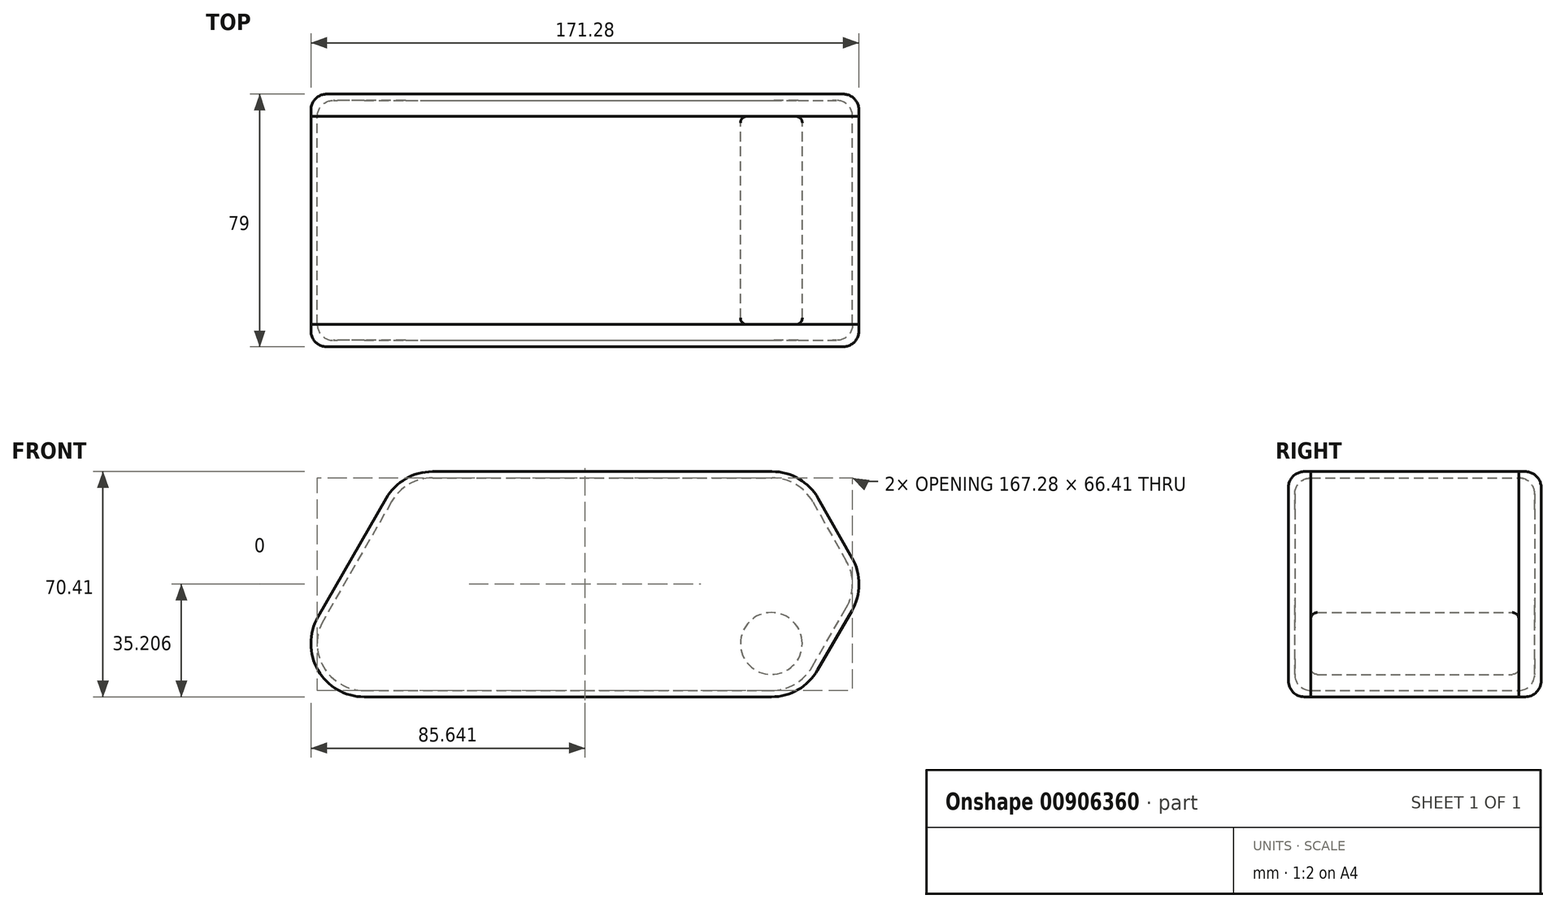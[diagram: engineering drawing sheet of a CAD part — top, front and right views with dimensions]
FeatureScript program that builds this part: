
annotation { "Feature Type Name" : "Feature", "Feature Type Description" : "" }
export const myFeature = defineFeature(function(context is Context, id is Id, definition is map)
    precondition{}
    {
        {
            var Q0;
            Q0=qCreatedBy(makeId("Front.planeOp"),FACE);
            var sketch = newSketch(context, id + "F0", { "sketchPlane" : qUnion([Q0])});
            skCircle(sketch, "E0.1.0.0", {"center": v(20, 0) * mm, "radius": 9.67 * mm});
            skCircle(sketch, "E0.1.1.0", {"center": v(30.7, 18.54) * mm, "radius": 9.67 * mm});
            skCircle(sketch, "E0.2.0.0", {"center": v(41.2, 0) * mm, "radius": 9.67 * mm});
            skCircle(sketch, "E0.2.1.0", {"center": v(51.9, 18.54) * mm, "radius": 9.67 * mm});
            skCircle(sketch, "E0.2.2.0", {"center": v(62.6, 37.07) * mm, "radius": 9.67 * mm});
            skCircle(sketch, "E0.3.0.0", {"center": v(62.41, 0) * mm, "radius": 9.67 * mm});
            skCircle(sketch, "E0.3.1.0", {"center": v(73.11, 18.54) * mm, "radius": 9.67 * mm});
            skCircle(sketch, "E0.3.2.0", {"center": v(83.82, 37.07) * mm, "radius": 9.67 * mm});
            skCircle(sketch, "E0.4.0.0", {"center": v(83.62, 0) * mm, "radius": 9.67 * mm});
            skCircle(sketch, "E0.4.1.0", {"center": v(94.32, 18.54) * mm, "radius": 9.67 * mm});
            skCircle(sketch, "E0.4.2.0", {"center": v(105.02, 37.07) * mm, "radius": 9.67 * mm});
            skCircle(sketch, "E0.5.0.0", {"center": v(104.83, 0) * mm, "radius": 9.67 * mm});
            skCircle(sketch, "E0.5.1.0", {"center": v(115.53, 18.54) * mm, "radius": 9.67 * mm});
            skCircle(sketch, "E0.5.2.0", {"center": v(126.23, 37.07) * mm, "radius": 9.67 * mm});
            skCircle(sketch, "E0.6.0.0", {"center": v(126.03, 0) * mm, "radius": 9.67 * mm});
            skCircle(sketch, "E0.6.1.0", {"center": v(136.74, 18.54) * mm, "radius": 9.67 * mm});
            skCircle(sketch, "E0.6.2.0", {"center": v(147.44, 37.07) * mm, "radius": 9.67 * mm});
            skCircle(sketch, "E0.7.0.0", {"center": v(147.24, 0) * mm, "radius": 9.67 * mm});
            skCircle(sketch, "E0.7.1.0", {"center": v(157.94, 18.54) * mm, "radius": 9.67 * mm});
            skLineSegment(sketch, "E0.direction1", {"start": v(0, 0) * mm, "end": v(20, 0) * mm, "construction": true});
            skLineSegment(sketch, "E0.direction2", {"start": v(0, 0) * mm, "end": v(10.55, 18.27) * mm, "construction": true});
            skCircle(sketch, "E1.1.0.0", {"center": v(41.3, 37.05) * mm, "radius": 9.67 * mm});
            skLineSegment(sketch, "E1.direction1", {"start": v(62.6, 37.07) * mm, "end": v(41.3, 37.05) * mm, "construction": true});
            skSolve(sketch);
        }
        {
            var Q0;
            Q0=qCreatedBy(makeId("Front.planeOp"),FACE);
            var sketch = newSketch(context, id + "F1", { "sketchPlane" : qUnion([Q0])});
            skArc(sketch, "E2.0", {"start": v(41.3, 46.72) * mm, "mid": v(36.46, 45.42) * mm, "end": v(32.92, 41.87) * mm});
            skArc(sketch, "E3.0", {"start": v(11.62, 4.82) * mm, "mid": v(11.63, -4.84) * mm, "end": v(20, -9.67) * mm});
            skArc(sketch, "E4.0", {"start": v(147.24, -9.67) * mm, "mid": v(152.07, -8.37) * mm, "end": v(155.61, -4.83) * mm});
            skArc(sketch, "E5.0", {"start": v(166.32, 13.7) * mm, "mid": v(167.61, 18.5) * mm, "end": v(166.35, 23.3) * mm});
            skArc(sketch, "E6.0", {"start": v(155.85, 41.84) * mm, "mid": v(152.3, 45.43) * mm, "end": v(147.44, 46.74) * mm});
            skLineSegment(sketch, "E7", {"start": v(32.92, 41.87) * mm, "end": v(11.62, 4.82) * mm});
            skLineSegment(sketch, "E8", {"start": v(41.3, 46.72) * mm, "end": v(147.44, 46.74) * mm});
            skLineSegment(sketch, "E9", {"start": v(155.85, 41.84) * mm, "end": v(166.35, 23.3) * mm});
            skLineSegment(sketch, "E10", {"start": v(155.61, -4.83) * mm, "end": v(166.32, 13.7) * mm});
            skLineSegment(sketch, "E11", {"start": v(20, -9.67) * mm, "end": v(147.24, -9.67) * mm});
            skArc(sketch, "E12.0", {"start": v(41.3, 51.72) * mm, "mid": v(33.96, 49.75) * mm, "end": v(28.59, 44.37) * mm});
            skLineSegment(sketch, "E12.1", {"start": v(28.59, 44.37) * mm, "end": v(7.28, 7.31) * mm});
            skLineSegment(sketch, "E12.2", {"start": v(41.3, 51.72) * mm, "end": v(147.43, 51.74) * mm});
            skArc(sketch, "E12.3", {"start": v(7.28, 7.31) * mm, "mid": v(7.3, -7.35) * mm, "end": v(20, -14.67) * mm});
            skLineSegment(sketch, "E12.4", {"start": v(20, -14.67) * mm, "end": v(147.24, -14.67) * mm});
            skArc(sketch, "E12.5", {"start": v(147.24, -14.67) * mm, "mid": v(154.57, -12.7) * mm, "end": v(159.94, -7.33) * mm});
            skArc(sketch, "E12.6", {"start": v(160.2, 44.3) * mm, "mid": v(154.82, 49.75) * mm, "end": v(147.43, 51.74) * mm});
            skLineSegment(sketch, "E12.7", {"start": v(160.2, 44.3) * mm, "end": v(170.7, 25.77) * mm});
            skArc(sketch, "E12.8", {"start": v(170.65, 11.2) * mm, "mid": v(172.61, 18.48) * mm, "end": v(170.7, 25.77) * mm});
            skLineSegment(sketch, "E12.9", {"start": v(159.94, -7.33) * mm, "end": v(170.65, 11.2) * mm});
            skArc(sketch, "E13.0", {"start": v(41.3, 53.72) * mm, "mid": v(32.96, 51.48) * mm, "end": v(26.85, 45.36) * mm});
            skLineSegment(sketch, "E13.1", {"start": v(26.85, 45.36) * mm, "end": v(5.55, 8.3) * mm});
            skLineSegment(sketch, "E13.2", {"start": v(41.3, 53.72) * mm, "end": v(147.43, 53.74) * mm});
            skArc(sketch, "E13.3", {"start": v(5.55, 8.3) * mm, "mid": v(5.57, -8.35) * mm, "end": v(20, -16.67) * mm});
            skLineSegment(sketch, "E13.4", {"start": v(20, -16.67) * mm, "end": v(147.24, -16.67) * mm});
            skArc(sketch, "E13.5", {"start": v(147.24, -16.67) * mm, "mid": v(155.57, -14.44) * mm, "end": v(161.68, -8.33) * mm});
            skArc(sketch, "E13.6", {"start": v(161.94, 45.3) * mm, "mid": v(155.83, 51.47) * mm, "end": v(147.43, 53.74) * mm});
            skLineSegment(sketch, "E13.7", {"start": v(161.94, 45.3) * mm, "end": v(172.44, 26.75) * mm});
            skArc(sketch, "E13.8", {"start": v(172.38, 10.2) * mm, "mid": v(174.61, 18.47) * mm, "end": v(172.44, 26.75) * mm});
            skLineSegment(sketch, "E13.9", {"start": v(161.68, -8.33) * mm, "end": v(172.38, 10.2) * mm});
            skSolve(sketch);
        }
        {
            var Q0;
            Q0=makeQuery(id+"F1.imprint","IMPRINT",FACE,{"disambiguationData":[TD([[makeQuery(id+"F1.imprint","IMPRINT",EDGE,{"derivedFrom":sQuery(id+"F1.wireOp",EDGE,"E12.0")}),-1.0]])]});
            extrude(context, id + "F2", {"entities" : qUnion([Q0]), "depth" : 65 * mm, "offsetDistance" : 25 * mm});
        }
        {
            var Q0;
            Q0=makeQuery(id+"F0.imprint","IMPRINT",FACE,{"disambiguationData":[TD([[makeQuery(id+"F0.imprint","IMPRINT",EDGE,{"derivedFrom":sQuery(id+"F0.wireOp",EDGE,"E0.7.0.0")}),1.0]])]});
            extrude(context, id + "F3", {"entities" : qUnion([Q0]), "depth" : 65 * mm, "offsetDistance" : 25 * mm});
        }
        {
            var Q0;
            Q0=makeQuery(id+"F3.opExtrude","CAP_FACE",FACE,{"disambiguationData":[OSD([sQuery(id+"F0.wireOp",EDGE,"E0.7.0.0")])],"isStart":false});
            var Q1;
            Q1=makeQuery(id+"F3.opExtrude","CAP_FACE",FACE,{"disambiguationData":[OSD([sQuery(id+"F0.wireOp",EDGE,"E0.7.0.0")])],"isStart":true});
            fillet(context, id + "F4", {"entities" : qUnion([Q0, Q1]), "radius" : 2 * mm, "tangentPropagation" : true, "allowEdgeOverflow" : false});
        }
        {
            var Q0;
            Q0=makeQuery(id+"F2.opExtrude","CAP_FACE",FACE,{"disambiguationData":[OSD([sQuery(id+"F1.wireOp",EDGE,"E12.0"),sQuery(id+"F1.wireOp",EDGE,"E12.1"),sQuery(id+"F1.wireOp",EDGE,"E12.2"),sQuery(id+"F1.wireOp",EDGE,"E12.3"),sQuery(id+"F1.wireOp",EDGE,"E12.4"),sQuery(id+"F1.wireOp",EDGE,"E12.5"),sQuery(id+"F1.wireOp",EDGE,"E12.6"),sQuery(id+"F1.wireOp",EDGE,"E12.7"),sQuery(id+"F1.wireOp",EDGE,"E12.8"),sQuery(id+"F1.wireOp",EDGE,"E12.9"),sQuery(id+"F1.wireOp",EDGE,"E13.0"),sQuery(id+"F1.wireOp",EDGE,"E13.1"),sQuery(id+"F1.wireOp",EDGE,"E13.2"),sQuery(id+"F1.wireOp",EDGE,"E13.3"),sQuery(id+"F1.wireOp",EDGE,"E13.4"),sQuery(id+"F1.wireOp",EDGE,"E13.5"),sQuery(id+"F1.wireOp",EDGE,"E13.6"),sQuery(id+"F1.wireOp",EDGE,"E13.7"),sQuery(id+"F1.wireOp",EDGE,"E13.8"),sQuery(id+"F1.wireOp",EDGE,"E13.9")])],"isStart":true});
            var sketch = newSketch(context, id + "F5", { "sketchPlane" : qUnion([Q0])});
            skArc(sketch, "E14.0.0", {"start": v(-161.68, -8.33) * mm, "mid": v(-155.57, -14.44) * mm, "end": v(-147.24, -16.67) * mm});
            skLineSegment(sketch, "E14.0.1", {"start": v(-147.24, -16.67) * mm, "end": v(-20, -16.67) * mm});
            skArc(sketch, "E14.0.2", {"start": v(-20, -16.67) * mm, "mid": v(-5.57, -8.35) * mm, "end": v(-5.55, 8.3) * mm});
            skLineSegment(sketch, "E14.0.3", {"start": v(-5.55, 8.3) * mm, "end": v(-26.85, 45.36) * mm});
            skArc(sketch, "E14.0.4", {"start": v(-26.85, 45.36) * mm, "mid": v(-32.96, 51.48) * mm, "end": v(-41.3, 53.72) * mm});
            skLineSegment(sketch, "E14.0.5", {"start": v(-41.3, 53.72) * mm, "end": v(-147.43, 53.74) * mm});
            skArc(sketch, "E14.0.6", {"start": v(-147.43, 53.74) * mm, "mid": v(-155.83, 51.47) * mm, "end": v(-161.94, 45.3) * mm});
            skLineSegment(sketch, "E14.0.7", {"start": v(-161.94, 45.3) * mm, "end": v(-172.44, 26.75) * mm});
            skArc(sketch, "E14.0.8", {"start": v(-172.44, 26.75) * mm, "mid": v(-174.61, 18.47) * mm, "end": v(-172.38, 10.2) * mm});
            skLineSegment(sketch, "E14.0.9", {"start": v(-172.38, 10.2) * mm, "end": v(-161.68, -8.33) * mm});
            skLineSegment(sketch, "E15.0", {"start": v(-20, -14.67) * mm, "end": v(-147.24, -14.67) * mm});
            skArc(sketch, "E16.0", {"start": v(-147.24, -14.67) * mm, "mid": v(-154.57, -12.7) * mm, "end": v(-159.94, -7.33) * mm});
            skLineSegment(sketch, "E17.0", {"start": v(-159.94, -7.33) * mm, "end": v(-170.65, 11.2) * mm});
            skArc(sketch, "E18.0", {"start": v(-170.65, 11.2) * mm, "mid": v(-172.61, 18.48) * mm, "end": v(-170.7, 25.77) * mm});
            skLineSegment(sketch, "E19.0", {"start": v(-160.2, 44.3) * mm, "end": v(-170.7, 25.77) * mm});
            skArc(sketch, "E20.0", {"start": v(-160.2, 44.3) * mm, "mid": v(-154.82, 49.75) * mm, "end": v(-147.43, 51.74) * mm});
            skLineSegment(sketch, "E21.0", {"start": v(-41.3, 51.72) * mm, "end": v(-147.43, 51.74) * mm});
            skArc(sketch, "E22.0", {"start": v(-41.3, 51.72) * mm, "mid": v(-33.96, 49.75) * mm, "end": v(-28.59, 44.37) * mm});
            skArc(sketch, "E23.0", {"start": v(-7.28, 7.31) * mm, "mid": v(-7.3, -7.35) * mm, "end": v(-20, -14.67) * mm});
            skLineSegment(sketch, "E24.0", {"start": v(-28.59, 44.37) * mm, "end": v(-7.28, 7.31) * mm});
            skSolve(sketch);
        }
        {
            var Q0;
            Q0=makeQuery(id+"F5.imprint","IMPRINT",FACE,{"disambiguationData":[TD([[makeQuery(id+"F5.imprint","IMPRINT",EDGE,{"derivedFrom":sQuery(id+"F5.wireOp",EDGE,"E14.0.0")}),-1.0]])]});
            extrude(context, id + "F6", {"entities" : qUnion([Q0]), "depth" : 5 * mm, "offsetDistance" : 25 * mm});
        }
        {
            var Q0;
            Q0=makeQuery(id+"F6.opExtrude","CAP_FACE",FACE,{"disambiguationData":[OSD([sQuery(id+"F5.wireOp",EDGE,"E14.0.0"),sQuery(id+"F5.wireOp",EDGE,"E14.0.1"),sQuery(id+"F5.wireOp",EDGE,"E14.0.2"),sQuery(id+"F5.wireOp",EDGE,"E14.0.3"),sQuery(id+"F5.wireOp",EDGE,"E14.0.4"),sQuery(id+"F5.wireOp",EDGE,"E14.0.5"),sQuery(id+"F5.wireOp",EDGE,"E14.0.6"),sQuery(id+"F5.wireOp",EDGE,"E14.0.7"),sQuery(id+"F5.wireOp",EDGE,"E14.0.8"),sQuery(id+"F5.wireOp",EDGE,"E14.0.9"),sQuery(id+"F5.wireOp",EDGE,"E15.0"),sQuery(id+"F5.wireOp",EDGE,"E16.0"),sQuery(id+"F5.wireOp",EDGE,"E17.0"),sQuery(id+"F5.wireOp",EDGE,"E18.0"),sQuery(id+"F5.wireOp",EDGE,"E19.0"),sQuery(id+"F5.wireOp",EDGE,"E20.0"),sQuery(id+"F5.wireOp",EDGE,"E21.0"),sQuery(id+"F5.wireOp",EDGE,"E22.0"),sQuery(id+"F5.wireOp",EDGE,"E23.0"),sQuery(id+"F5.wireOp",EDGE,"E24.0")])],"isStart":false});
            var sketch = newSketch(context, id + "F7", { "sketchPlane" : qUnion([Q0])});
            skArc(sketch, "E25.0.0", {"start": v(-161.68, -8.33) * mm, "mid": v(-155.57, -14.44) * mm, "end": v(-147.24, -16.67) * mm});
            skLineSegment(sketch, "E25.0.1", {"start": v(-147.24, -16.67) * mm, "end": v(-20, -16.67) * mm});
            skArc(sketch, "E25.0.2", {"start": v(-20, -16.67) * mm, "mid": v(-5.57, -8.35) * mm, "end": v(-5.55, 8.3) * mm});
            skLineSegment(sketch, "E25.0.3", {"start": v(-5.55, 8.3) * mm, "end": v(-26.85, 45.36) * mm});
            skArc(sketch, "E25.0.4", {"start": v(-26.85, 45.36) * mm, "mid": v(-32.96, 51.48) * mm, "end": v(-41.3, 53.72) * mm});
            skLineSegment(sketch, "E25.0.5", {"start": v(-41.3, 53.72) * mm, "end": v(-147.43, 53.74) * mm});
            skArc(sketch, "E25.0.6", {"start": v(-147.43, 53.74) * mm, "mid": v(-155.83, 51.47) * mm, "end": v(-161.94, 45.3) * mm});
            skLineSegment(sketch, "E25.0.7", {"start": v(-161.94, 45.3) * mm, "end": v(-172.44, 26.75) * mm});
            skArc(sketch, "E25.0.8", {"start": v(-172.44, 26.75) * mm, "mid": v(-174.61, 18.47) * mm, "end": v(-172.38, 10.2) * mm});
            skLineSegment(sketch, "E25.0.9", {"start": v(-172.38, 10.2) * mm, "end": v(-161.68, -8.33) * mm});
            skSolve(sketch);
        }
        {
            var Q0;
            Q0 = qSketchRegion(id + "F7", true);
            extrude(context, id + "F8", {"entities" : qUnion([Q0]), "operationType" : NewBodyOperationType.ADD, "depth" : 2 * mm, "offsetDistance" : 25 * mm});
        }
        {
            var Q0;
            Q0=makeQuery(id+"F8.opExtrude","CAP_FACE",FACE,{"disambiguationData":[OSD([sQuery(id+"F7.wireOp",EDGE,"E25.0.0"),sQuery(id+"F7.wireOp",EDGE,"E25.0.1"),sQuery(id+"F7.wireOp",EDGE,"E25.0.2"),sQuery(id+"F7.wireOp",EDGE,"E25.0.3"),sQuery(id+"F7.wireOp",EDGE,"E25.0.4"),sQuery(id+"F7.wireOp",EDGE,"E25.0.5"),sQuery(id+"F7.wireOp",EDGE,"E25.0.6"),sQuery(id+"F7.wireOp",EDGE,"E25.0.7"),sQuery(id+"F7.wireOp",EDGE,"E25.0.8"),sQuery(id+"F7.wireOp",EDGE,"E25.0.9")])],"isStart":false});
            fillet(context, id + "F9", {"entities" : qUnion([Q0]), "radius" : 5 * mm, "tangentPropagation" : true, "allowEdgeOverflow" : false});
        }
        {
            var Q0;
            Q0=makeQuery(id+"F8.opExtrude","CAP_FACE",FACE,{"disambiguationData":[OSD([sQuery(id+"F7.wireOp",EDGE,"E25.0.0"),sQuery(id+"F7.wireOp",EDGE,"E25.0.1"),sQuery(id+"F7.wireOp",EDGE,"E25.0.2"),sQuery(id+"F7.wireOp",EDGE,"E25.0.3"),sQuery(id+"F7.wireOp",EDGE,"E25.0.4"),sQuery(id+"F7.wireOp",EDGE,"E25.0.5"),sQuery(id+"F7.wireOp",EDGE,"E25.0.6"),sQuery(id+"F7.wireOp",EDGE,"E25.0.7"),sQuery(id+"F7.wireOp",EDGE,"E25.0.8"),sQuery(id+"F7.wireOp",EDGE,"E25.0.9")])],"isStart":true});
            fillet(context, id + "F10", {"entities" : qUnion([Q0]), "radius" : 5 * mm, "tangentPropagation" : true, "allowEdgeOverflow" : false});
        }
        {
            var Q0;
            Q0=qCreatedBy(makeId("Front.planeOp"),FACE);
            cPlane(context, id + "F11", {"entities" : qUnion([Q0]), "cplaneType" : CPlaneType.OFFSET, "offset" : 32.5 * mm, "width" : 150 * mm, "height" : 150 * mm});
        }
        {
            var Q0;
            Q0=makeQuery(id+"F6.opExtrude","SWEPT_BODY",BODY,{"disambiguationData":[OSD([sQuery(id+"F5.wireOp",EDGE,"E14.0.0"),sQuery(id+"F5.wireOp",EDGE,"E14.0.1"),sQuery(id+"F5.wireOp",EDGE,"E14.0.2"),sQuery(id+"F5.wireOp",EDGE,"E14.0.3"),sQuery(id+"F5.wireOp",EDGE,"E14.0.4"),sQuery(id+"F5.wireOp",EDGE,"E14.0.5"),sQuery(id+"F5.wireOp",EDGE,"E14.0.6"),sQuery(id+"F5.wireOp",EDGE,"E14.0.7"),sQuery(id+"F5.wireOp",EDGE,"E14.0.8"),sQuery(id+"F5.wireOp",EDGE,"E14.0.9"),sQuery(id+"F5.wireOp",EDGE,"E15.0"),sQuery(id+"F5.wireOp",EDGE,"E16.0"),sQuery(id+"F5.wireOp",EDGE,"E17.0"),sQuery(id+"F5.wireOp",EDGE,"E18.0"),sQuery(id+"F5.wireOp",EDGE,"E19.0"),sQuery(id+"F5.wireOp",EDGE,"E20.0"),sQuery(id+"F5.wireOp",EDGE,"E21.0"),sQuery(id+"F5.wireOp",EDGE,"E22.0"),sQuery(id+"F5.wireOp",EDGE,"E23.0"),sQuery(id+"F5.wireOp",EDGE,"E24.0")])]});
            var Q1;
            Q1=qCreatedBy(id+"F11.planeOp",FACE);
            mirror(context, id + "F12", {"entities" : qUnion([Q0]), "mirrorPlane" : qUnion([Q1])});
        }
    });
